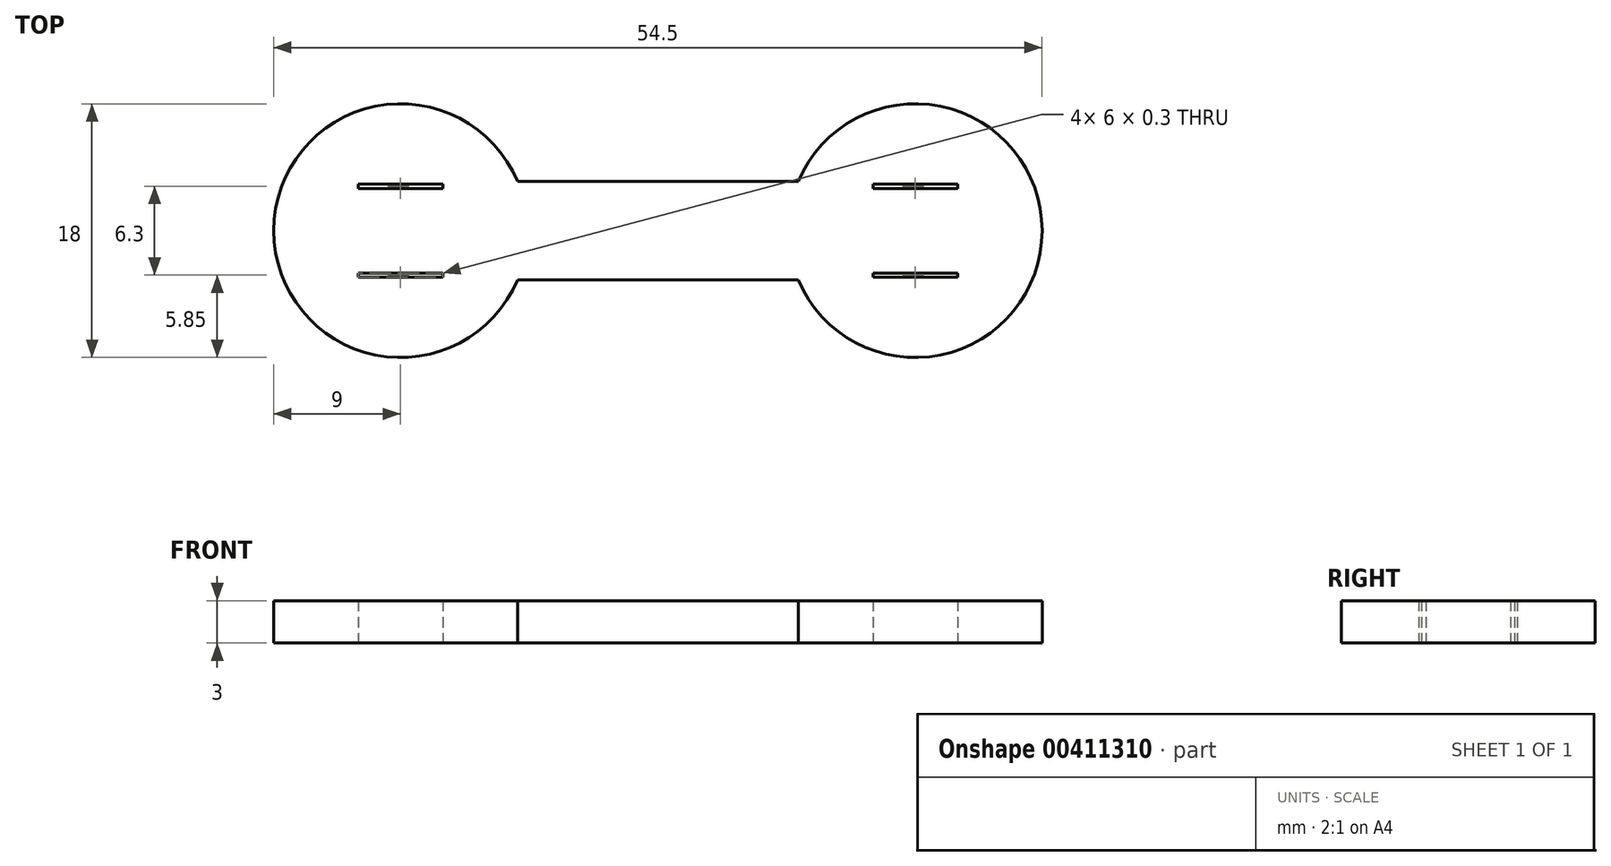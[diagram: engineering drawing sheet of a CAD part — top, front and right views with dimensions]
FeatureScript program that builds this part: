
annotation { "Feature Type Name" : "Feature", "Feature Type Description" : "" }
export const myFeature = defineFeature(function(context is Context, id is Id, definition is map)
    precondition{}
    {
        {
            var Q0;
            Q0=qCreatedBy(makeId("Top.planeOp"),FACE);
            var sketch = newSketch(context, id + "F0", { "sketchPlane" : qUnion([Q0])});
            skArc(sketch, "E0", {"start": v(8.3, 3.5) * mm, "mid": v(-9, 0) * mm, "end": v(8.3, -3.5) * mm});
            skLineSegment(sketch, "E1.bottom", {"start": v(8, 3.5) * mm, "end": v(28.21, 3.5) * mm});
            skLineSegment(sketch, "E1.top", {"start": v(8, -3.5) * mm, "end": v(28.21, -3.5) * mm});
            skArc(sketch, "E2", {"start": v(28.21, -3.5) * mm, "mid": v(45.5, 0) * mm, "end": v(28.21, 3.5) * mm});
            skLineSegment(sketch, "E3.bottom", {"start": v(-3, 3.3) * mm, "end": v(3, 3.3) * mm});
            skLineSegment(sketch, "E3.top", {"start": v(-3, 3) * mm, "end": v(3, 3) * mm});
            skLineSegment(sketch, "E3.left", {"start": v(-3, 3.3) * mm, "end": v(-3, 3) * mm});
            skLineSegment(sketch, "E3.right", {"start": v(3, 3.3) * mm, "end": v(3, 3) * mm});
            skLineSegment(sketch, "E4.bottom", {"start": v(-3, -3) * mm, "end": v(3, -3) * mm});
            skLineSegment(sketch, "E4.top", {"start": v(-3, -3.3) * mm, "end": v(3, -3.3) * mm});
            skLineSegment(sketch, "E4.left", {"start": v(-3, -3) * mm, "end": v(-3, -3.3) * mm});
            skLineSegment(sketch, "E4.right", {"start": v(3, -3) * mm, "end": v(3, -3.3) * mm});
            skLineSegment(sketch, "E5.bottom", {"start": v(33.5, 3.3) * mm, "end": v(39.5, 3.3) * mm});
            skLineSegment(sketch, "E5.top", {"start": v(33.5, 3) * mm, "end": v(39.5, 3) * mm});
            skLineSegment(sketch, "E5.left", {"start": v(33.5, 3.3) * mm, "end": v(33.5, 3) * mm});
            skLineSegment(sketch, "E5.right", {"start": v(39.5, 3.3) * mm, "end": v(39.5, 3) * mm});
            skLineSegment(sketch, "E6.bottom", {"start": v(33.5, -3) * mm, "end": v(39.5, -3) * mm});
            skLineSegment(sketch, "E6.top", {"start": v(33.5, -3.3) * mm, "end": v(39.5, -3.3) * mm});
            skLineSegment(sketch, "E6.left", {"start": v(33.5, -3) * mm, "end": v(33.5, -3.3) * mm});
            skLineSegment(sketch, "E6.right", {"start": v(39.5, -3) * mm, "end": v(39.5, -3.3) * mm});
            skSolve(sketch);
        }
        {
            var Q0;
            {var subQ0=sQuery(id+"F0.wireOp",EDGE,"E0");Q0=makeQuery(id+"F0.imprint","IMPRINT",FACE,{"disambiguationData":[TD([[makeQuery(id+"F0.imprint","IMPRINT",EDGE,{"derivedFrom":subQ0}),1.0]])]});}
            extrude(context, id + "F1", {"entities" : qUnion([Q0]), "depth" : 3 * mm});
        }
    });
